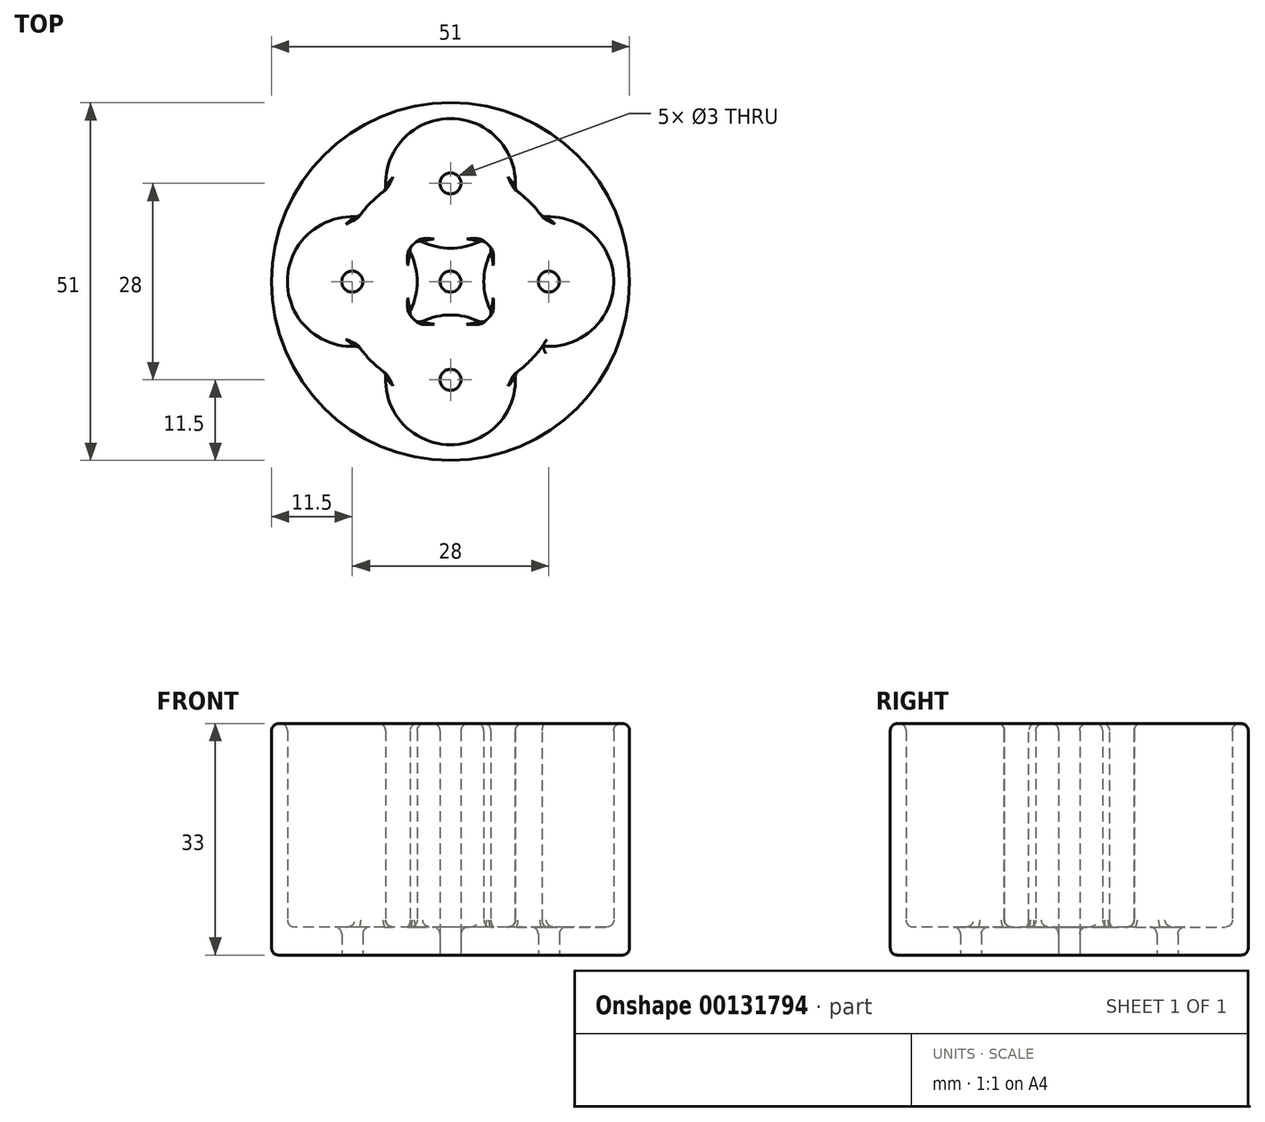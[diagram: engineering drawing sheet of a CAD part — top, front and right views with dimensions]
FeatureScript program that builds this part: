
annotation { "Feature Type Name" : "Feature", "Feature Type Description" : "" }
export const myFeature = defineFeature(function(context is Context, id is Id, definition is map)
    precondition{}
    {
        {
            var Q0;
            Q0=qCreatedBy(makeId("Top.planeOp"),FACE);
            var sketch = newSketch(context, id + "F0", { "sketchPlane" : qUnion([Q0])});
            skCircle(sketch, "E0", {"center": v(0, 0) * mm, "radius": 1.5 * mm});
            skCircle(sketch, "E1", {"center": v(0, 14) * mm, "radius": 9.25 * mm});
            skCircle(sketch, "E2", {"center": v(0, -14) * mm, "radius": 9.25 * mm});
            skCircle(sketch, "E3", {"center": v(-14, 0) * mm, "radius": 9.25 * mm});
            skCircle(sketch, "E4", {"center": v(14, 0) * mm, "radius": 9.25 * mm});
            skCircle(sketch, "E5", {"center": v(0, 0) * mm, "radius": 25.5 * mm});
            skCircle(sketch, "E6", {"center": v(-14, 0) * mm, "radius": 1.5 * mm});
            skCircle(sketch, "E7", {"center": v(14, 0) * mm, "radius": 1.5 * mm});
            skCircle(sketch, "E8", {"center": v(0, 14) * mm, "radius": 1.5 * mm});
            skCircle(sketch, "E9", {"center": v(0, -14) * mm, "radius": 1.5 * mm});
            skSolve(sketch);
        }
        {
            var Q0;
            Q0=makeQuery(id+"F0.imprint","IMPRINT",FACE,{"disambiguationData":[TD([[makeQuery(id+"F0.imprint","IMPRINT",EDGE,{"derivedFrom":sQuery(id+"F0.wireOp",EDGE,"E0")}),-1.0]])]});
            var Q1;
            Q1=makeQuery(id+"F0.imprint","IMPRINT",FACE,{"disambiguationData":[TD([[makeQuery(id+"F0.imprint","IMPRINT",EDGE,{"derivedFrom":sQuery(id+"F0.wireOp",EDGE,"E1")}),1.0]])]});
            var Q2;
            Q2=makeQuery(id+"F0.imprint","IMPRINT",FACE,{"disambiguationData":[TD([[makeQuery(id+"F0.imprint","IMPRINT",EDGE,{"derivedFrom":sQuery(id+"F0.wireOp",EDGE,"E4")}),1.0]])]});
            var Q3;
            Q3=makeQuery(id+"F0.imprint","IMPRINT",FACE,{"disambiguationData":[TD([[makeQuery(id+"F0.imprint","IMPRINT",EDGE,{"derivedFrom":sQuery(id+"F0.wireOp",EDGE,"E2")}),1.0]])]});
            var Q4;
            Q4=makeQuery(id+"F0.imprint","IMPRINT",FACE,{"disambiguationData":[TD([[makeQuery(id+"F0.imprint","IMPRINT",EDGE,{"derivedFrom":sQuery(id+"F0.wireOp",EDGE,"E3")}),1.0]])]});
            extrude(context, id + "F1", {"entities" : qUnion([Q0, Q1, Q2, Q3, Q4]), "depth" : 4 * mm});
        }
        {
            var Q0;
            Q0 = qSketchRegion(id + "F0", true);
            extrude(context, id + "F2", {"entities" : qUnion([Q0]), "operationType" : NewBodyOperationType.ADD, "depth" : 33 * mm});
        }
        {
            var Q0;
            {var subQ0=sQuery(id+"F0.wireOp",EDGE,"E8");Q0=makeQuery(id+"FKi44YuD8fVXP33_2.opBoolean","SPLIT",FACE,{"disambiguationData":[TD([makeQuery(id+"F1.opExtrude","SWEPT_FACE",FACE,{"disambiguationData":[OSD([subQ0])]})])],"derivedFrom":makeQuery(id+"F1.opExtrude","CAP_FACE",FACE,{"disambiguationData":[OSD([sQuery(id+"F0.wireOp",EDGE,"E0"),sQuery(id+"F0.wireOp",EDGE,"E5"),sQuery(id+"F0.wireOp",EDGE,"E6"),sQuery(id+"F0.wireOp",EDGE,"E7"),subQ0,sQuery(id+"F0.wireOp",EDGE,"E9")])],"isStart":false})});}
            var Q1;
            {var subQ0=sQuery(id+"F0.wireOp",EDGE,"E7");Q1=makeQuery(id+"FKi44YuD8fVXP33_2.opBoolean","SPLIT",FACE,{"disambiguationData":[TD([makeQuery(id+"F1.opExtrude","SWEPT_FACE",FACE,{"disambiguationData":[OSD([subQ0])]})])],"derivedFrom":makeQuery(id+"F1.opExtrude","CAP_FACE",FACE,{"disambiguationData":[OSD([sQuery(id+"F0.wireOp",EDGE,"E0"),sQuery(id+"F0.wireOp",EDGE,"E5"),sQuery(id+"F0.wireOp",EDGE,"E6"),subQ0,sQuery(id+"F0.wireOp",EDGE,"E8"),sQuery(id+"F0.wireOp",EDGE,"E9")])],"isStart":false})});}
            var Q2;
            {var subQ0=sQuery(id+"F0.wireOp",EDGE,"E9");Q2=makeQuery(id+"FKi44YuD8fVXP33_2.opBoolean","SPLIT",FACE,{"disambiguationData":[TD([makeQuery(id+"F1.opExtrude","SWEPT_FACE",FACE,{"disambiguationData":[OSD([subQ0])]})])],"derivedFrom":makeQuery(id+"F1.opExtrude","CAP_FACE",FACE,{"disambiguationData":[OSD([sQuery(id+"F0.wireOp",EDGE,"E0"),sQuery(id+"F0.wireOp",EDGE,"E5"),sQuery(id+"F0.wireOp",EDGE,"E6"),sQuery(id+"F0.wireOp",EDGE,"E7"),sQuery(id+"F0.wireOp",EDGE,"E8"),subQ0])],"isStart":false})});}
            var Q3;
            {var subQ0=sQuery(id+"F0.wireOp",EDGE,"E6");Q3=makeQuery(id+"FKi44YuD8fVXP33_2.opBoolean","SPLIT",FACE,{"disambiguationData":[TD([makeQuery(id+"F1.opExtrude","SWEPT_FACE",FACE,{"disambiguationData":[OSD([subQ0])]})])],"derivedFrom":makeQuery(id+"F1.opExtrude","CAP_FACE",FACE,{"disambiguationData":[OSD([sQuery(id+"F0.wireOp",EDGE,"E0"),sQuery(id+"F0.wireOp",EDGE,"E5"),subQ0,sQuery(id+"F0.wireOp",EDGE,"E7"),sQuery(id+"F0.wireOp",EDGE,"E8"),sQuery(id+"F0.wireOp",EDGE,"E9")])],"isStart":false})});}
            fillet(context, id + "F3", {"entities" : qUnion([Q0, Q1, Q2, Q3]), "radius" : 1 * mm, "tangentPropagation" : true, "allowEdgeOverflow" : false});
        }
        {
            var Q0;
            Q0=makeQuery(id+"FFGCTITDjTNYAHK_1.opFillet","SPLIT",FACE,{"disambiguationData":[OD(6.0)],"derivedFrom":makeQuery(id+"F2.opExtrude","CAP_FACE",FACE,{"disambiguationData":[OSD([sQuery(id+"F0.wireOp",EDGE,"E0"),sQuery(id+"F0.wireOp",EDGE,"E1"),sQuery(id+"F0.wireOp",EDGE,"E2"),sQuery(id+"F0.wireOp",EDGE,"E3"),sQuery(id+"F0.wireOp",EDGE,"E4"),sQuery(id+"F0.wireOp",EDGE,"E5")])],"isStart":false})});
            var sketch = newSketch(context, id + "F4", { "sketchPlane" : qUnion([Q0])});
            skCircle(sketch, "E10", {"center": v(0, 0) * mm, "radius": 7.5 * mm});
            skCircle(sketch, "E11", {"center": v(0, 0) * mm, "radius": 16 * mm});
            skSolve(sketch);
        }
        {
            var Q0;
            Q0=makeQuery(id+"F4.imprint","IMPRINT",FACE,{"disambiguationData":[TD([[makeQuery(id+"F4.imprint","IMPRINT",EDGE,{"derivedFrom":sQuery(id+"F4.wireOp",EDGE,"E10")}),-1.0]])]});
            extrude(context, id + "F5", {"entities" : qUnion([Q0]), "operationType" : NewBodyOperationType.REMOVE, "oppositeDirection" : true, "depth" : 29 * mm});
        }
        {
            var Q0;
            Q0=makeQuery(id+"F5.boolean.opBoolean","INTERSECT",EDGE,{"disambiguationData":[OD(0.0)],"derivedFrom":[makeQuery(id+"F2.opExtrude","SWEPT_FACE",FACE,{"disambiguationData":[OSD([sQuery(id+"F0.wireOp",EDGE,"E3")])]}),makeQuery(id+"F5.opExtrude","SWEPT_FACE",FACE,{"disambiguationData":[OSD([sQuery(id+"F4.wireOp",EDGE,"E11")])]})]});
            var Q1;
            Q1=makeQuery(id+"F5.boolean.opBoolean","INTERSECT",EDGE,{"disambiguationData":[OD(0.0)],"derivedFrom":[makeQuery(id+"F2.opExtrude","SWEPT_FACE",FACE,{"disambiguationData":[OSD([sQuery(id+"F0.wireOp",EDGE,"E1")])]}),makeQuery(id+"F5.opExtrude","SWEPT_FACE",FACE,{"disambiguationData":[OSD([sQuery(id+"F4.wireOp",EDGE,"E11")])]})]});
            var Q2;
            Q2=makeQuery(id+"F5.boolean.opBoolean","INTERSECT",EDGE,{"disambiguationData":[OD(1.0)],"derivedFrom":[makeQuery(id+"F2.opExtrude","SWEPT_FACE",FACE,{"disambiguationData":[OSD([sQuery(id+"F0.wireOp",EDGE,"E1")])]}),makeQuery(id+"F5.opExtrude","SWEPT_FACE",FACE,{"disambiguationData":[OSD([sQuery(id+"F4.wireOp",EDGE,"E11")])]})]});
            var Q3;
            Q3=makeQuery(id+"F5.boolean.opBoolean","INTERSECT",EDGE,{"disambiguationData":[OD(0.0)],"derivedFrom":[makeQuery(id+"F2.opExtrude","SWEPT_FACE",FACE,{"disambiguationData":[OSD([sQuery(id+"F0.wireOp",EDGE,"E4")])]}),makeQuery(id+"F5.opExtrude","SWEPT_FACE",FACE,{"disambiguationData":[OSD([sQuery(id+"F4.wireOp",EDGE,"E11")])]})]});
            var Q4;
            Q4=makeQuery(id+"F5.boolean.opBoolean","INTERSECT",EDGE,{"disambiguationData":[OD(1.0)],"derivedFrom":[makeQuery(id+"F2.opExtrude","SWEPT_FACE",FACE,{"disambiguationData":[OSD([sQuery(id+"F0.wireOp",EDGE,"E3")])]}),makeQuery(id+"F5.opExtrude","SWEPT_FACE",FACE,{"disambiguationData":[OSD([sQuery(id+"F4.wireOp",EDGE,"E11")])]})]});
            var Q5;
            Q5=makeQuery(id+"F5.boolean.opBoolean","INTERSECT",EDGE,{"disambiguationData":[OD(0.0)],"derivedFrom":[makeQuery(id+"F2.opExtrude","SWEPT_FACE",FACE,{"disambiguationData":[OSD([sQuery(id+"F0.wireOp",EDGE,"E2")])]}),makeQuery(id+"F5.opExtrude","SWEPT_FACE",FACE,{"disambiguationData":[OSD([sQuery(id+"F4.wireOp",EDGE,"E11")])]})]});
            var Q6;
            Q6=makeQuery(id+"F5.boolean.opBoolean","INTERSECT",EDGE,{"disambiguationData":[OD(1.0)],"derivedFrom":[makeQuery(id+"F2.opExtrude","SWEPT_FACE",FACE,{"disambiguationData":[OSD([sQuery(id+"F0.wireOp",EDGE,"E2")])]}),makeQuery(id+"F5.opExtrude","SWEPT_FACE",FACE,{"disambiguationData":[OSD([sQuery(id+"F4.wireOp",EDGE,"E11")])]})]});
            fillet(context, id + "F6", {"entities" : qUnion([Q0, Q1, Q2, Q3, Q4, Q5, Q6]), "radius" : 1 * mm, "tangentPropagation" : true, "allowEdgeOverflow" : false});
        }
        {
            var Q0;
            Q0=makeQuery(id+"F5.boolean.opBoolean","INTERSECT",EDGE,{"disambiguationData":[OD(1.0)],"derivedFrom":[makeQuery(id+"F2.opExtrude","SWEPT_FACE",FACE,{"disambiguationData":[OSD([sQuery(id+"F0.wireOp",EDGE,"E2")])]}),makeQuery(id+"F5.opExtrude","SWEPT_FACE",FACE,{"disambiguationData":[OSD([sQuery(id+"F4.wireOp",EDGE,"E10")])]})]});
            var Q1;
            Q1=makeQuery(id+"F5.boolean.opBoolean","INTERSECT",EDGE,{"disambiguationData":[OD(0.0)],"derivedFrom":[makeQuery(id+"F2.opExtrude","SWEPT_FACE",FACE,{"disambiguationData":[OSD([sQuery(id+"F0.wireOp",EDGE,"E2")])]}),makeQuery(id+"F5.opExtrude","SWEPT_FACE",FACE,{"disambiguationData":[OSD([sQuery(id+"F4.wireOp",EDGE,"E10")])]})]});
            var Q2;
            Q2=makeQuery(id+"F5.boolean.opBoolean","INTERSECT",EDGE,{"disambiguationData":[OD(0.0)],"derivedFrom":[makeQuery(id+"F2.opExtrude","SWEPT_FACE",FACE,{"disambiguationData":[OSD([sQuery(id+"F0.wireOp",EDGE,"E3")])]}),makeQuery(id+"F5.opExtrude","SWEPT_FACE",FACE,{"disambiguationData":[OSD([sQuery(id+"F4.wireOp",EDGE,"E10")])]})]});
            var Q3;
            Q3=makeQuery(id+"F5.boolean.opBoolean","INTERSECT",EDGE,{"disambiguationData":[OD(0.0)],"derivedFrom":[makeQuery(id+"F2.opExtrude","SWEPT_FACE",FACE,{"disambiguationData":[OSD([sQuery(id+"F0.wireOp",EDGE,"E1")])]}),makeQuery(id+"F5.opExtrude","SWEPT_FACE",FACE,{"disambiguationData":[OSD([sQuery(id+"F4.wireOp",EDGE,"E10")])]})]});
            var Q4;
            Q4=makeQuery(id+"F5.boolean.opBoolean","INTERSECT",EDGE,{"disambiguationData":[OD(1.0)],"derivedFrom":[makeQuery(id+"F2.opExtrude","SWEPT_FACE",FACE,{"disambiguationData":[OSD([sQuery(id+"F0.wireOp",EDGE,"E1")])]}),makeQuery(id+"F5.opExtrude","SWEPT_FACE",FACE,{"disambiguationData":[OSD([sQuery(id+"F4.wireOp",EDGE,"E10")])]})]});
            var Q5;
            Q5=makeQuery(id+"F5.boolean.opBoolean","INTERSECT",EDGE,{"disambiguationData":[OD(1.0)],"derivedFrom":[makeQuery(id+"F2.opExtrude","SWEPT_FACE",FACE,{"disambiguationData":[OSD([sQuery(id+"F0.wireOp",EDGE,"E4")])]}),makeQuery(id+"F5.opExtrude","SWEPT_FACE",FACE,{"disambiguationData":[OSD([sQuery(id+"F4.wireOp",EDGE,"E10")])]})]});
            var Q6;
            Q6=makeQuery(id+"F5.boolean.opBoolean","INTERSECT",EDGE,{"disambiguationData":[OD(0.0)],"derivedFrom":[makeQuery(id+"F2.opExtrude","SWEPT_FACE",FACE,{"disambiguationData":[OSD([sQuery(id+"F0.wireOp",EDGE,"E4")])]}),makeQuery(id+"F5.opExtrude","SWEPT_FACE",FACE,{"disambiguationData":[OSD([sQuery(id+"F4.wireOp",EDGE,"E10")])]})]});
            var Q7;
            Q7=makeQuery(id+"F5.boolean.opBoolean","INTERSECT",EDGE,{"disambiguationData":[OD(1.0)],"derivedFrom":[makeQuery(id+"F2.opExtrude","SWEPT_FACE",FACE,{"disambiguationData":[OSD([sQuery(id+"F0.wireOp",EDGE,"E3")])]}),makeQuery(id+"F5.opExtrude","SWEPT_FACE",FACE,{"disambiguationData":[OSD([sQuery(id+"F4.wireOp",EDGE,"E10")])]})]});
            fillet(context, id + "F7", {"entities" : qUnion([Q0, Q1, Q2, Q3, Q4, Q5, Q6, Q7]), "radius" : 1 * mm, "tangentPropagation" : true, "allowEdgeOverflow" : false});
        }
        {
            var Q0;
            {var subQ0=sQuery(id+"F0.wireOp",EDGE,"E3");var subQ1=sQuery(id+"F0.wireOp",EDGE,"E2");var subQ2=sQuery(id+"F0.wireOp",EDGE,"E1");var subQ3=sQuery(id+"F0.wireOp",EDGE,"E5");var subQ4=sQuery(id+"F0.wireOp",EDGE,"E4");Q0=makeQuery(id+"F5.boolean.opBoolean","SPLIT",FACE,{"disambiguationData":[TD([makeQuery(id+"F1.opExtrude","SWEPT_FACE",FACE,{"disambiguationData":[OSD([subQ3])]})])],"derivedFrom":makeQuery(id+"F2.opExtrude","CAP_FACE",FACE,{"disambiguationData":[OSD([sQuery(id+"F0.wireOp",EDGE,"E0"),subQ2,subQ1,subQ0,subQ4,subQ3])],"isStart":false})});}
            var Q1;
            {var subQ0=sQuery(id+"F0.wireOp",EDGE,"E1");var subQ1=sQuery(id+"F0.wireOp",EDGE,"E0");var subQ2=sQuery(id+"F0.wireOp",EDGE,"E2");var subQ3=sQuery(id+"F0.wireOp",EDGE,"E3");var subQ4=sQuery(id+"F0.wireOp",EDGE,"E4");Q1=makeQuery(id+"F5.boolean.opBoolean","SPLIT",FACE,{"disambiguationData":[TD([makeQuery(id+"F1.opExtrude","SWEPT_FACE",FACE,{"disambiguationData":[OSD([subQ1])]})])],"derivedFrom":makeQuery(id+"F2.opExtrude","CAP_FACE",FACE,{"disambiguationData":[OSD([subQ1,subQ0,subQ2,subQ3,subQ4,sQuery(id+"F0.wireOp",EDGE,"E5")])],"isStart":false})});}
            var Q2;
            Q2=makeQuery(id+"F1.opExtrude","CAP_EDGE",EDGE,{"disambiguationData":[OSD([sQuery(id+"F0.wireOp",EDGE,"E5")])],"isStart":true});
            fillet(context, id + "F8", {"entities" : qUnion([Q0, Q1, Q2]), "radius" : 1 * mm, "tangentPropagation" : true, "allowEdgeOverflow" : false});
        }
    });
